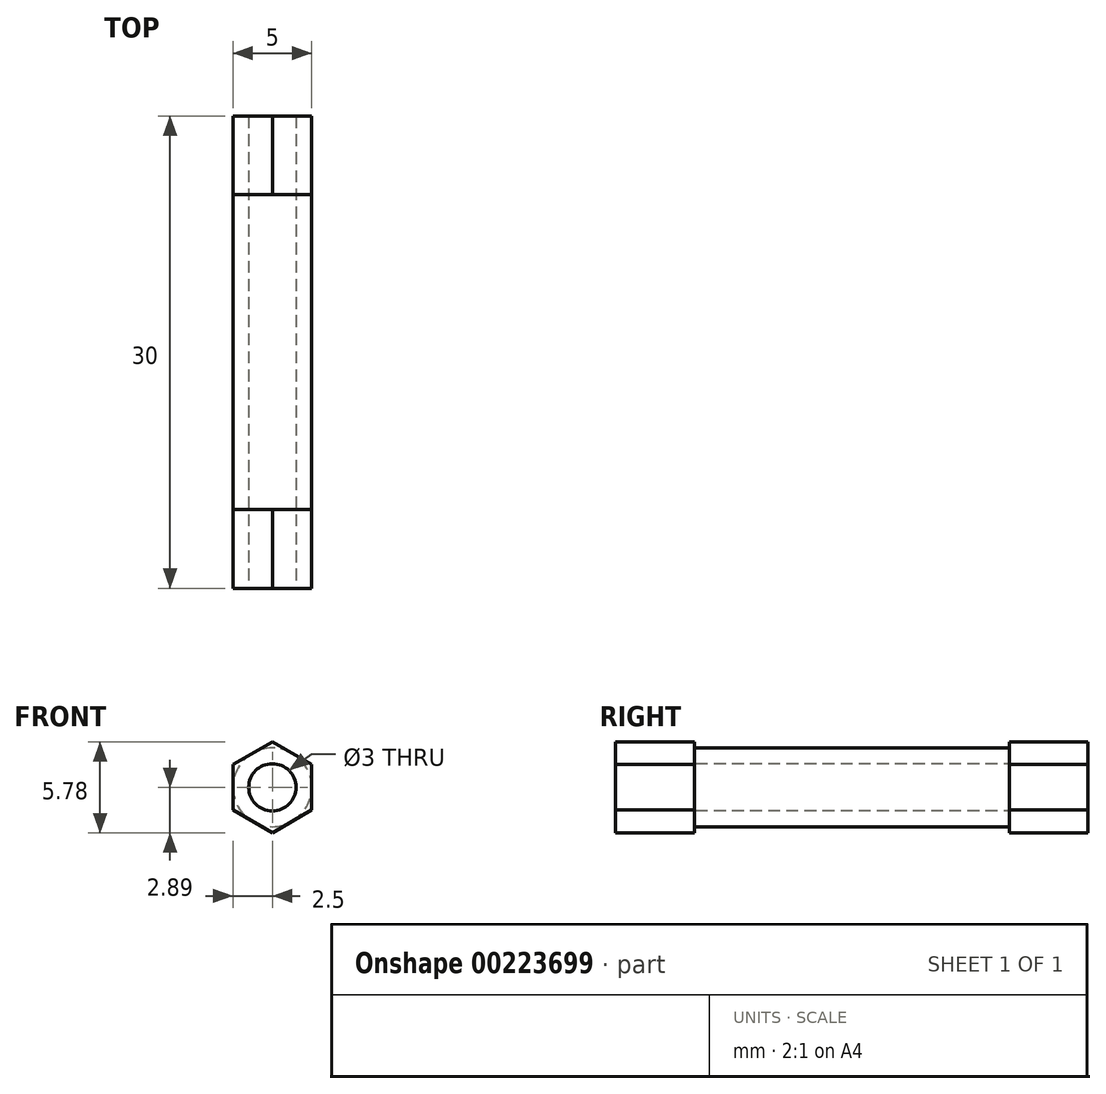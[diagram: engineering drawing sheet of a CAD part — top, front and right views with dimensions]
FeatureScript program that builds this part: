
annotation { "Feature Type Name" : "Feature", "Feature Type Description" : "" }
export const myFeature = defineFeature(function(context is Context, id is Id, definition is map)
    precondition{}
    {
        {
            assignVariable(context, id + "F0", {"name" : "StandoffHeight", "anyValue" : 30});
        }
        {
            var Q0;
            Q0=qCreatedBy(makeId("Front.planeOp"),FACE);
            var sketch = newSketch(context, id + "F1", { "sketchPlane" : qUnion([Q0])});
            skCircle(sketch, "E0", {"center": v(0, 0) * mm, "radius": 2.5 * mm});
            skCircle(sketch, "E1.cCircle", {"center": v(0, 0) * mm, "radius": 2.5 * mm, "construction": true});
            skPoint(sketch, "E1.0.midPoint", {"position": v(-1.25, 2.17) * mm});
            skSolve(sketch);
        }
        {
            var Q0;
            Q0=makeQuery(id+"F1.imprint","IMPRINT",FACE,{"disambiguationData":[TD([[makeQuery(id+"F1.imprint","IMPRINT",EDGE,{"derivedFrom":sQuery(id+"F1.wireOp",EDGE,"E0")}),1.0]])]});
            var Q1;
            Q1=qSketchRegion(id+"F3",true);
            extrude(context, id + "F2", {"entities" : qUnion([Q0, Q1]), "depth" : (getVariable(context, 'StandoffHeight') / 2 - 5) * mm});
        }
        {
            var Q0;
            Q0=makeQuery(id+"F2.opExtrude","CAP_FACE",FACE,{"disambiguationData":[OSD([sQuery(id+"F1.wireOp",EDGE,"E0")])],"isStart":false});
            var sketch = newSketch(context, id + "F3", { "sketchPlane" : qUnion([Q0])});
            skCircle(sketch, "E2.cCircle", {"center": v(0, 0) * mm, "radius": 2.5 * mm, "construction": true});
            skLineSegment(sketch, "E2.0", {"start": v(-2.5, -1.44) * mm, "end": v(-2.5, 1.44) * mm});
            skLineSegment(sketch, "E2.1", {"start": v(-2.5, 1.44) * mm, "end": v(0, 2.89) * mm});
            skLineSegment(sketch, "E2.2", {"start": v(0, 2.89) * mm, "end": v(2.5, 1.44) * mm});
            skLineSegment(sketch, "E2.3", {"start": v(2.5, 1.44) * mm, "end": v(2.5, -1.44) * mm});
            skLineSegment(sketch, "E2.4", {"start": v(2.5, -1.44) * mm, "end": v(0, -2.89) * mm});
            skLineSegment(sketch, "E2.5", {"start": v(0, -2.89) * mm, "end": v(-2.5, -1.44) * mm});
            skPoint(sketch, "E2.0.midPoint", {"position": v(-2.5, 0) * mm});
            skSolve(sketch);
        }
        {
            var Q0;
            Q0=qSketchRegion(id+"F3",true);
            extrude(context, id + "F4", {"entities" : qUnion([Q0]), "operationType" : NewBodyOperationType.ADD, "depth" : 5 * mm});
        }
        {
            var Q0;
            Q0=sQuery(id+"F1.wireOp",VERTEX,"E0.center");
            var Q1;
            Q1=makeQuery(id+"F2.opExtrude","SWEPT_BODY",BODY,{"disambiguationData":[OSD([sQuery(id+"F1.wireOp",EDGE,"E0")])]});
            hole(context, id + "F5", {"style" : HoleStyle.SIMPLE, "endStyle" : HoleEndStyle.THROUGH, "oppositeDirection" : true, "holeDiameter" : 3 * mm, "locations" : qUnion([Q0]), "scope" : qUnion([Q1]), "isTappedThrough" : true, "startStyle" : HoleStartStyle.PART});
        }
        {
            var Q0;
            Q0=makeQuery(id+"F2.opExtrude","SWEPT_BODY",BODY,{"disambiguationData":[OSD([sQuery(id+"F1.wireOp",EDGE,"E0")])]});
            var Q1;
            Q1=makeQuery(id+"F1.imprint","IMPRINT",FACE,{"disambiguationData":[TD([[makeQuery(id+"F1.imprint","IMPRINT",EDGE,{"derivedFrom":sQuery(id+"F1.wireOp",EDGE,"E0")}),1.0]])]});
            mirror(context, id + "F6", {"operationType" : NewBodyOperationType.ADD, "entities" : qUnion([Q0]), "mirrorPlane" : qUnion([Q1])});
        }
    });
